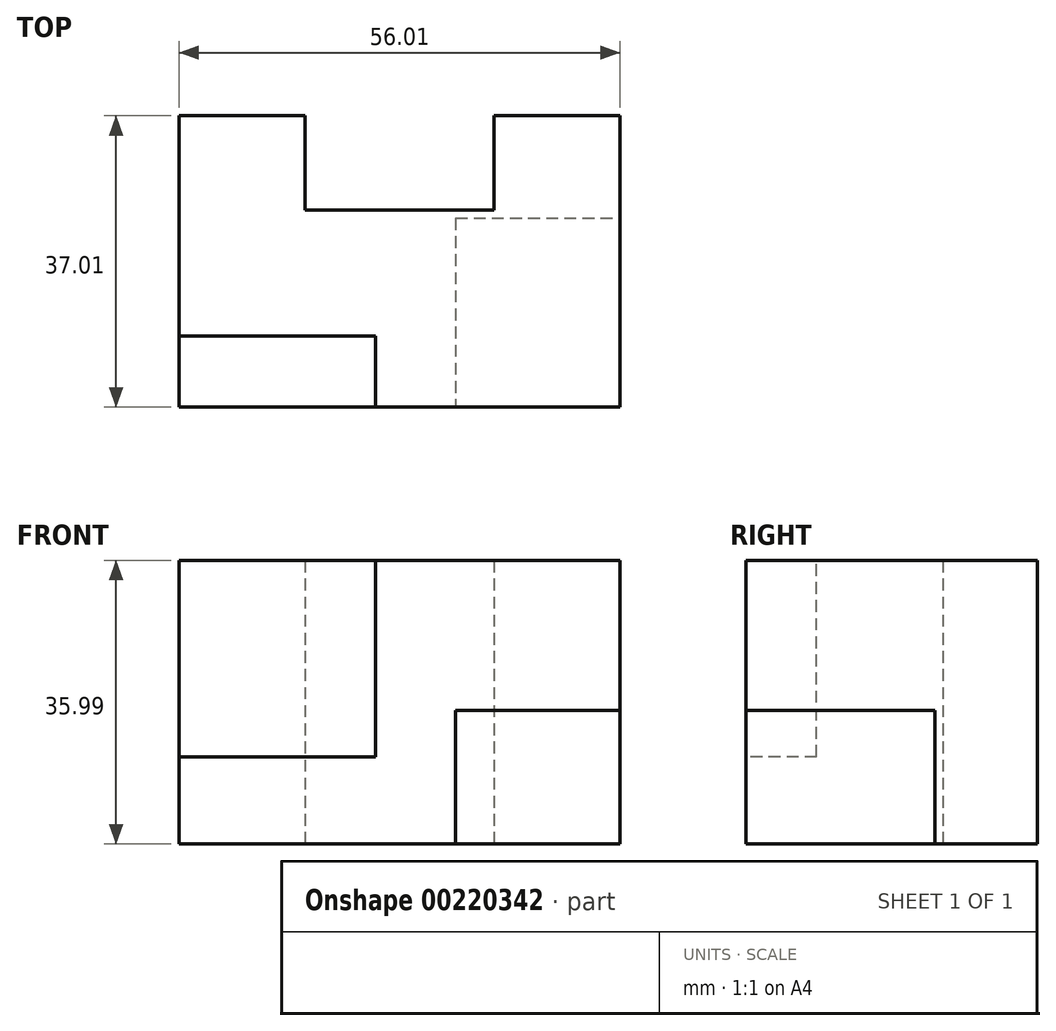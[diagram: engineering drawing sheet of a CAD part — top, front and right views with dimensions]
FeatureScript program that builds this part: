
annotation { "Feature Type Name" : "Feature", "Feature Type Description" : "" }
export const myFeature = defineFeature(function(context is Context, id is Id, definition is map)
    precondition{}
    {
        {
            var Q0;
            Q0=qCreatedBy(makeId("Top.planeOp"),FACE);
            var sketch = newSketch(context, id + "F0", { "sketchPlane" : qUnion([Q0])});
            skLineSegment(sketch, "E0.bottom", {"start": v(0, 0) * mm, "end": v(16, 0) * mm});
            skLineSegment(sketch, "E0.top", {"start": v(0, -37) * mm, "end": v(56, -37) * mm});
            skLineSegment(sketch, "E0.left", {"start": v(0, 0) * mm, "end": v(0, -37) * mm});
            skLineSegment(sketch, "E0.right", {"start": v(56, 0) * mm, "end": v(56, -37) * mm});
            skLineSegment(sketch, "E1.0", {"start": v(16, 0) * mm, "end": v(16, -11.99) * mm});
            skLineSegment(sketch, "E2.0", {"start": v(40, 0) * mm, "end": v(40, -11.99) * mm});
            skLineSegment(sketch, "E3.0", {"start": v(16, -11.99) * mm, "end": v(40, -11.99) * mm});
            skLineSegment(sketch, "E4.trimOffspring", {"start": v(40, 0) * mm, "end": v(56, 0) * mm});
            skSolve(sketch);
        }
        {
            var Q0;
            Q0=makeQuery(id+"F0.imprint","IMPRINT",FACE,{"disambiguationData":[TD([[makeQuery(id+"F0.imprint","IMPRINT",EDGE,{"derivedFrom":sQuery(id+"F0.wireOp",EDGE,"E0.bottom")}),-1.0]])]});
            extrude(context, id + "F1", {"entities" : qUnion([Q0]), "depth" : 36 * mm});
        }
        {
            var Q0;
            Q0=makeQuery(id+"F1.opExtrude","CAP_FACE",FACE,{"disambiguationData":[OSD([sQuery(id+"F0.wireOp",EDGE,"E0.bottom"),sQuery(id+"F0.wireOp",EDGE,"E0.top"),sQuery(id+"F0.wireOp",EDGE,"E0.left"),sQuery(id+"F0.wireOp",EDGE,"E0.right"),sQuery(id+"F0.wireOp",EDGE,"E1.0"),sQuery(id+"F0.wireOp",EDGE,"E2.0"),sQuery(id+"F0.wireOp",EDGE,"E3.0"),sQuery(id+"F0.wireOp",EDGE,"E4.trimOffspring")])],"isStart":false});
            var sketch = newSketch(context, id + "F2", { "sketchPlane" : qUnion([Q0])});
            skLineSegment(sketch, "E5.bottom", {"start": v(0, -37) * mm, "end": v(24.97, -37) * mm});
            skLineSegment(sketch, "E5.top", {"start": v(0, -28.02) * mm, "end": v(24.97, -28.02) * mm});
            skLineSegment(sketch, "E5.left", {"start": v(0, -37) * mm, "end": v(0, -28.02) * mm});
            skLineSegment(sketch, "E5.right", {"start": v(24.97, -37) * mm, "end": v(24.97, -28.02) * mm});
            skSolve(sketch);
        }
        {
            var Q0;
            Q0 = qSketchRegion(id + "F2", true);
            extrude(context, id + "F3", {"entities" : qUnion([Q0]), "operationType" : NewBodyOperationType.REMOVE, "oppositeDirection" : true, "depth" : 24.94 * mm});
        }
        {
            var Q0;
            Q0=makeQuery(id+"F1.opExtrude","SWEPT_FACE",FACE,{"disambiguationData":[OSD([sQuery(id+"F0.wireOp",EDGE,"E0.top")])]});
            var sketch = newSketch(context, id + "F4", { "sketchPlane" : qUnion([Q0])});
            skLineSegment(sketch, "E6.bottom", {"start": v(56, 0) * mm, "end": v(35.15, 0) * mm});
            skLineSegment(sketch, "E6.top", {"start": v(56, 16.94) * mm, "end": v(35.15, 16.94) * mm});
            skLineSegment(sketch, "E6.left", {"start": v(56, 0) * mm, "end": v(56, 16.94) * mm});
            skLineSegment(sketch, "E6.right", {"start": v(35.15, 0) * mm, "end": v(35.15, 16.94) * mm});
            skSolve(sketch);
        }
        {
            var Q0;
            Q0 = qSketchRegion(id + "F4", true);
            extrude(context, id + "F5", {"entities" : qUnion([Q0]), "operationType" : NewBodyOperationType.REMOVE, "oppositeDirection" : true, "depth" : 24 * mm});
        }
    });
